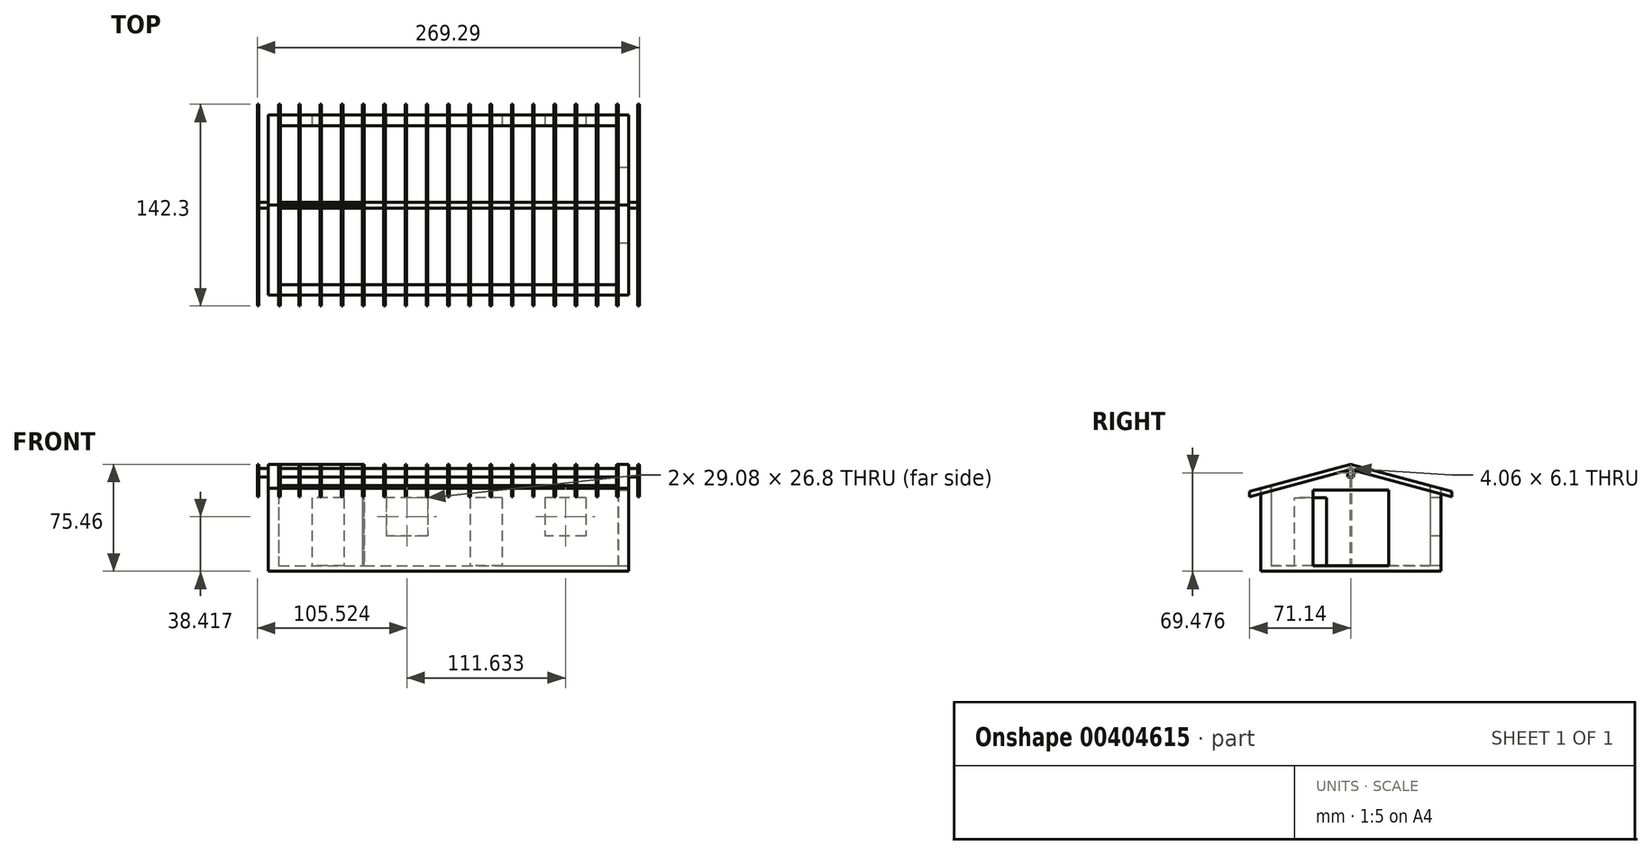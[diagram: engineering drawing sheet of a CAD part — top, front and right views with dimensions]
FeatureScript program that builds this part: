
annotation { "Feature Type Name" : "Feature", "Feature Type Description" : "" }
export const myFeature = defineFeature(function(context is Context, id is Id, definition is map)
    precondition{}
    {
        {
            var Q0;
            Q0=qCreatedBy(makeId("Top.planeOp"),FACE);
            var sketch = newSketch(context, id + "F0", { "sketchPlane" : qUnion([Q0])});
            skLineSegment(sketch, "E0.bottom", {"start": v(0, 0) * mm, "end": v(-254, 0) * mm});
            skLineSegment(sketch, "E0.top", {"start": v(0, 127) * mm, "end": v(-254, 127) * mm});
            skLineSegment(sketch, "E0.left", {"start": v(0, 0) * mm, "end": v(0, 127) * mm});
            skLineSegment(sketch, "E0.right", {"start": v(-254, 0) * mm, "end": v(-254, 127) * mm});
            skLineSegment(sketch, "E1.bottom", {"start": v(-7.37, 7.37) * mm, "end": v(-186.39, 7.37) * mm});
            skLineSegment(sketch, "E1.top", {"start": v(-7.37, 119.63) * mm, "end": v(-186.39, 119.63) * mm});
            skLineSegment(sketch, "E1.left", {"start": v(-7.37, 7.37) * mm, "end": v(-7.37, 119.63) * mm});
            skLineSegment(sketch, "E1.right", {"start": v(-246.63, 7.37) * mm, "end": v(-246.63, 62.86) * mm});
            skLineSegment(sketch, "E2", {"start": v(-186.39, 119.63) * mm, "end": v(-186.39, 7.37) * mm});
            skLineSegment(sketch, "E3", {"start": v(-187.53, 7.37) * mm, "end": v(-187.53, 62.86) * mm});
            skLineSegment(sketch, "E4", {"start": v(-187.53, 64) * mm, "end": v(-246.63, 64) * mm});
            skLineSegment(sketch, "E5", {"start": v(-246.63, 62.86) * mm, "end": v(-187.53, 62.86) * mm});
            skLineSegment(sketch, "E6.trimOffspring", {"start": v(-187.53, 64) * mm, "end": v(-187.53, 119.63) * mm});
            skLineSegment(sketch, "E7.trimOffspring", {"start": v(-187.53, 7.37) * mm, "end": v(-246.63, 7.37) * mm});
            skLineSegment(sketch, "E8.trimOffspring", {"start": v(-187.53, 119.63) * mm, "end": v(-246.63, 119.63) * mm});
            skLineSegment(sketch, "E9.trimOffspring", {"start": v(-246.63, 64) * mm, "end": v(-246.63, 119.63) * mm});
            skSolve(sketch);
        }
        {
            var Q0;
            Q0 = qSketchRegion(id + "F0", true);
            var Q1;
            Q1=makeQuery(id+"F0.imprint","IMPRINT",FACE,{"disambiguationData":[TD([[makeQuery(id+"F0.imprint","IMPRINT",EDGE,{"derivedFrom":sQuery(id+"F0.wireOp",EDGE,"E1.bottom")}),-1.0]])]});
            var Q2;
            Q2=makeQuery(id+"F0.imprint","IMPRINT",FACE,{"disambiguationData":[TD([[makeQuery(id+"F0.imprint","IMPRINT",EDGE,{"derivedFrom":sQuery(id+"F0.wireOp",EDGE,"E4")}),-1.0]])]});
            var Q3;
            Q3=makeQuery(id+"F0.imprint","IMPRINT",FACE,{"disambiguationData":[TD([[makeQuery(id+"F0.imprint","IMPRINT",EDGE,{"derivedFrom":sQuery(id+"F0.wireOp",EDGE,"E1.right")}),-1.0]])]});
            extrude(context, id + "F1", {"entities" : qUnion([Q0, Q1, Q2, Q3]), "depth" : 3.8 * mm});
        }
        {
            var Q0;
            Q0 = qSketchRegion(id + "F0", true);
            extrude(context, id + "F2", {"entities" : qUnion([Q0]), "operationType" : NewBodyOperationType.ADD, "depth" : 76.2 * mm});
        }
        {
            var Q0;
            Q0=qCreatedBy(makeId("Right.planeOp"),FACE);
            var sketch = newSketch(context, id + "F3", { "sketchPlane" : qUnion([Q0])});
            skLineSegment(sketch, "E10", {"start": v(0, 58.42) * mm, "end": v(63.5, 75.43) * mm});
            skLineSegment(sketch, "E11", {"start": v(63.5, 75.43) * mm, "end": v(127, 58.42) * mm});
            skLineSegment(sketch, "E12", {"start": v(127, 58.42) * mm, "end": v(127, 0) * mm});
            skLineSegment(sketch, "E13", {"start": v(127, 0) * mm, "end": v(0, 0) * mm});
            skLineSegment(sketch, "E14", {"start": v(0, 0) * mm, "end": v(0, 58.42) * mm});
            skLineSegment(sketch, "E15", {"start": v(0, 58.42) * mm, "end": v(0, 83.76) * mm});
            skLineSegment(sketch, "E16", {"start": v(0, 83.76) * mm, "end": v(127, 83.76) * mm});
            skLineSegment(sketch, "E17", {"start": v(127, 83.76) * mm, "end": v(127, 58.42) * mm});
            skLineSegment(sketch, "E18.bottom", {"start": v(36.83, 3.81) * mm, "end": v(90.17, 3.81) * mm});
            skLineSegment(sketch, "E18.top", {"start": v(36.83, 57.15) * mm, "end": v(90.17, 57.15) * mm});
            skLineSegment(sketch, "E18.left", {"start": v(36.83, 3.81) * mm, "end": v(36.83, 57.15) * mm});
            skLineSegment(sketch, "E18.right", {"start": v(90.17, 3.81) * mm, "end": v(90.17, 57.15) * mm});
            skLineSegment(sketch, "E19.bottom", {"start": v(61.47, 72.52) * mm, "end": v(65.53, 72.52) * mm});
            skLineSegment(sketch, "E19.top", {"start": v(61.47, 66.43) * mm, "end": v(65.53, 66.43) * mm});
            skLineSegment(sketch, "E19.left", {"start": v(61.47, 72.52) * mm, "end": v(61.47, 66.43) * mm});
            skLineSegment(sketch, "E19.right", {"start": v(65.53, 72.52) * mm, "end": v(65.53, 66.43) * mm});
            skSolve(sketch);
        }
        {
            var Q0;
            Q0=makeQuery(id+"F3.imprint","IMPRINT",FACE,{"disambiguationData":[TD([[makeQuery(id+"F3.imprint","IMPRINT",EDGE,{"derivedFrom":sQuery(id+"F3.wireOp",EDGE,"E10")}),1.0]])]});
            extrude(context, id + "F4", {"entities" : qUnion([Q0]), "operationType" : NewBodyOperationType.REMOVE, "oppositeDirection" : true, "depth" : 254 * mm});
        }
        {
            var Q0;
            Q0=makeQuery(id+"F3.imprint","IMPRINT",FACE,{"disambiguationData":[TD([[makeQuery(id+"F3.imprint","IMPRINT",EDGE,{"derivedFrom":sQuery(id+"F3.wireOp",EDGE,"CqusFpdj-rhDA-VQEZ-rAuY-6c3tKg3UXa0b.bottom")}),1.0]])]});
            var Q1;
            Q1=makeQuery(id+"F3.imprint","IMPRINT",FACE,{"disambiguationData":[TD([[makeQuery(id+"F3.imprint","IMPRINT",EDGE,{"derivedFrom":sQuery(id+"F3.wireOp",EDGE,"E18.bottom")}),1.0]])]});
            extrude(context, id + "F5", {"entities" : qUnion([Q0, Q1]), "operationType" : NewBodyOperationType.REMOVE, "oppositeDirection" : true, "depth" : 7.37 * mm});
        }
        {
            var Q0;
            Q0=qCreatedBy(makeId("Front.planeOp"),FACE);
            var sketch = newSketch(context, id + "F6", { "sketchPlane" : qUnion([Q0])});
            skLineSegment(sketch, "E20.bottom", {"start": v(-29.97, 51.82) * mm, "end": v(-59.06, 51.82) * mm});
            skLineSegment(sketch, "E20.top", {"start": v(-29.97, 25.02) * mm, "end": v(-59.06, 25.02) * mm});
            skLineSegment(sketch, "E20.left", {"start": v(-29.97, 51.82) * mm, "end": v(-29.97, 25.02) * mm});
            skLineSegment(sketch, "E20.right", {"start": v(-59.06, 51.82) * mm, "end": v(-59.06, 25.02) * mm});
            skLineSegment(sketch, "E21.bottom", {"start": v(-89.03, 51.82) * mm, "end": v(-111.63, 51.82) * mm});
            skLineSegment(sketch, "E21.top", {"start": v(-89.03, 3.81) * mm, "end": v(-111.63, 3.8) * mm});
            skLineSegment(sketch, "E21.left", {"start": v(-89.03, 51.82) * mm, "end": v(-89.03, 3.81) * mm});
            skLineSegment(sketch, "E21.right", {"start": v(-111.63, 51.82) * mm, "end": v(-111.63, 3.81) * mm});
            skLineSegment(sketch, "E22.bottom", {"start": v(-141.6, 51.82) * mm, "end": v(-170.69, 51.82) * mm});
            skLineSegment(sketch, "E22.top", {"start": v(-141.6, 25.02) * mm, "end": v(-170.69, 25.02) * mm});
            skLineSegment(sketch, "E22.left", {"start": v(-141.6, 51.82) * mm, "end": v(-141.6, 25.02) * mm});
            skLineSegment(sketch, "E22.right", {"start": v(-170.69, 51.82) * mm, "end": v(-170.69, 25.02) * mm});
            skLineSegment(sketch, "E23.bottom", {"start": v(-200.66, 51.82) * mm, "end": v(-223.27, 51.82) * mm});
            skLineSegment(sketch, "E23.top", {"start": v(-200.66, 3.81) * mm, "end": v(-223.27, 3.8) * mm});
            skLineSegment(sketch, "E23.left", {"start": v(-200.66, 51.82) * mm, "end": v(-200.66, 3.81) * mm});
            skLineSegment(sketch, "E23.right", {"start": v(-223.27, 51.82) * mm, "end": v(-223.27, 3.8) * mm});
            skSolve(sketch);
        }
        {
            var Q0;
            Q0 = qSketchRegion(id + "F6", true);
            extrude(context, id + "F7", {"entities" : qUnion([Q0]), "operationType" : NewBodyOperationType.REMOVE, "oppositeDirection" : true, "depth" : 127 * mm, "hasSecondDirection" : true, "secondDirectionOppositeDirection" : true, "secondDirectionDepth" : 119.38 * mm});
        }
        {
            var Q0;
            Q0=makeQuery(id+"F2.opExtrude","SWEPT_FACE",FACE,{"disambiguationData":[OSD([sQuery(id+"F0.wireOp",EDGE,"E2")])]});
            var sketch = newSketch(context, id + "F8", { "sketchPlane" : qUnion([Q0])});
            skLineSegment(sketch, "E24.bottom", {"start": v(23.88, 3.81) * mm, "end": v(46.48, 3.81) * mm});
            skLineSegment(sketch, "E24.top", {"start": v(23.88, 51.82) * mm, "end": v(46.48, 51.82) * mm});
            skLineSegment(sketch, "E24.left", {"start": v(23.88, 3.81) * mm, "end": v(23.88, 51.82) * mm});
            skLineSegment(sketch, "E24.right", {"start": v(46.48, 3.81) * mm, "end": v(46.48, 51.82) * mm});
            skSolve(sketch);
        }
        {
            var Q0;
            Q0 = qSketchRegion(id + "F8", true);
            extrude(context, id + "F9", {"entities" : qUnion([Q0]), "operationType" : NewBodyOperationType.REMOVE, "oppositeDirection" : true, "depth" : 1.27 * mm});
        }
        {
            var Q0;
            Q0=makeQuery(id+"F3.imprint","IMPRINT",FACE,{"disambiguationData":[TD([[makeQuery(id+"F3.imprint","IMPRINT",EDGE,{"derivedFrom":sQuery(id+"F3.wireOp",EDGE,"E19.bottom")}),-1.0]])]});
            extrude(context, id + "F10", {"entities" : qUnion([Q0]), "operationType" : NewBodyOperationType.ADD, "oppositeDirection" : true, "depth" : 261.62 * mm, "hasSecondDirection" : true, "secondDirectionOppositeDirection" : false, "secondDirectionDepth" : 7.62 * mm});
        }
        {
            var Q0;
            Q0=makeQuery(id+"F4.boolean.opBoolean","COPY",FACE,{"derivedFrom":makeQuery(id+"F4.opExtrude","SWEPT_FACE",FACE,{"disambiguationData":[OSD([sQuery(id+"F3.wireOp",EDGE,"E11")])]})});
            var sketch = newSketch(context, id + "F11", { "sketchPlane" : qUnion([Q0])});
            skLineSegment(sketch, "E25.bottom", {"start": v(7.62, 41.81) * mm, "end": v(6.48, 41.81) * mm});
            skLineSegment(sketch, "E25.top", {"start": v(7.62, 125.63) * mm, "end": v(6.48, 125.63) * mm});
            skLineSegment(sketch, "E25.left", {"start": v(7.62, 41.81) * mm, "end": v(7.62, 125.63) * mm});
            skLineSegment(sketch, "E25.right", {"start": v(6.48, 41.81) * mm, "end": v(6.48, 125.63) * mm});
            skLineSegment(sketch, "E26.bottom", {"start": v(-7.37, 41.81) * mm, "end": v(-8.5, 41.81) * mm});
            skLineSegment(sketch, "E26.top", {"start": v(-7.37, 125.63) * mm, "end": v(-8.5, 125.63) * mm});
            skLineSegment(sketch, "E26.left", {"start": v(-7.37, 41.81) * mm, "end": v(-7.37, 125.63) * mm});
            skLineSegment(sketch, "E26.right", {"start": v(-8.5, 41.81) * mm, "end": v(-8.5, 125.63) * mm});
            skLineSegment(sketch, "E27.bottom", {"start": v(-21.54, 41.81) * mm, "end": v(-22.68, 41.81) * mm});
            skLineSegment(sketch, "E27.top", {"start": v(-21.54, 125.63) * mm, "end": v(-22.68, 125.63) * mm});
            skLineSegment(sketch, "E27.left", {"start": v(-21.54, 41.81) * mm, "end": v(-21.54, 125.63) * mm});
            skLineSegment(sketch, "E27.right", {"start": v(-22.68, 41.81) * mm, "end": v(-22.68, 125.63) * mm});
            skLineSegment(sketch, "E28.bottom", {"start": v(-36.53, 41.81) * mm, "end": v(-37.67, 41.81) * mm});
            skLineSegment(sketch, "E28.top", {"start": v(-36.53, 125.63) * mm, "end": v(-37.67, 125.63) * mm});
            skLineSegment(sketch, "E28.left", {"start": v(-36.53, 41.81) * mm, "end": v(-36.53, 125.63) * mm});
            skLineSegment(sketch, "E28.right", {"start": v(-37.67, 41.81) * mm, "end": v(-37.67, 125.63) * mm});
            skLineSegment(sketch, "E29.bottom", {"start": v(-51.51, 41.81) * mm, "end": v(-52.65, 41.81) * mm});
            skLineSegment(sketch, "E29.top", {"start": v(-51.51, 125.63) * mm, "end": v(-52.65, 125.63) * mm});
            skLineSegment(sketch, "E29.left", {"start": v(-51.51, 41.81) * mm, "end": v(-51.51, 125.63) * mm});
            skLineSegment(sketch, "E29.right", {"start": v(-52.65, 41.81) * mm, "end": v(-52.65, 125.63) * mm});
            skLineSegment(sketch, "E30.bottom", {"start": v(-66.5, 41.81) * mm, "end": v(-67.64, 41.81) * mm});
            skLineSegment(sketch, "E30.top", {"start": v(-66.5, 125.63) * mm, "end": v(-67.64, 125.63) * mm});
            skLineSegment(sketch, "E30.left", {"start": v(-66.5, 41.81) * mm, "end": v(-66.5, 125.63) * mm});
            skLineSegment(sketch, "E30.right", {"start": v(-67.64, 41.81) * mm, "end": v(-67.64, 125.63) * mm});
            skLineSegment(sketch, "E31.bottom", {"start": v(-81.48, 41.81) * mm, "end": v(-82.63, 41.81) * mm});
            skLineSegment(sketch, "E31.top", {"start": v(-81.48, 125.63) * mm, "end": v(-82.63, 125.63) * mm});
            skLineSegment(sketch, "E31.left", {"start": v(-81.48, 41.81) * mm, "end": v(-81.48, 125.63) * mm});
            skLineSegment(sketch, "E31.right", {"start": v(-82.63, 41.81) * mm, "end": v(-82.63, 125.63) * mm});
            skLineSegment(sketch, "E32.bottom", {"start": v(-96.47, 41.81) * mm, "end": v(-97.61, 41.81) * mm});
            skLineSegment(sketch, "E32.top", {"start": v(-96.47, 125.63) * mm, "end": v(-97.61, 125.63) * mm});
            skLineSegment(sketch, "E32.left", {"start": v(-96.47, 41.81) * mm, "end": v(-96.47, 125.63) * mm});
            skLineSegment(sketch, "E32.right", {"start": v(-97.61, 41.81) * mm, "end": v(-97.61, 125.63) * mm});
            skLineSegment(sketch, "E33.bottom", {"start": v(-111.46, 41.81) * mm, "end": v(-112.6, 41.81) * mm});
            skLineSegment(sketch, "E33.top", {"start": v(-111.46, 125.63) * mm, "end": v(-112.6, 125.63) * mm});
            skLineSegment(sketch, "E33.left", {"start": v(-111.46, 41.81) * mm, "end": v(-111.46, 125.63) * mm});
            skLineSegment(sketch, "E33.right", {"start": v(-112.6, 41.81) * mm, "end": v(-112.6, 125.63) * mm});
            skLineSegment(sketch, "E34.bottom", {"start": v(-126.44, 41.81) * mm, "end": v(-127.58, 41.81) * mm});
            skLineSegment(sketch, "E34.top", {"start": v(-126.44, 125.63) * mm, "end": v(-127.58, 125.63) * mm});
            skLineSegment(sketch, "E34.left", {"start": v(-126.44, 41.81) * mm, "end": v(-126.44, 125.63) * mm});
            skLineSegment(sketch, "E34.right", {"start": v(-127.58, 41.81) * mm, "end": v(-127.58, 125.63) * mm});
            skLineSegment(sketch, "E35.bottom", {"start": v(-141.43, 41.81) * mm, "end": v(-142.57, 41.81) * mm});
            skLineSegment(sketch, "E35.top", {"start": v(-141.43, 125.63) * mm, "end": v(-142.57, 125.63) * mm});
            skLineSegment(sketch, "E35.left", {"start": v(-141.43, 41.81) * mm, "end": v(-141.43, 125.63) * mm});
            skLineSegment(sketch, "E35.right", {"start": v(-142.57, 41.81) * mm, "end": v(-142.57, 125.63) * mm});
            skLineSegment(sketch, "E36.bottom", {"start": v(-156.41, 41.81) * mm, "end": v(-157.56, 41.81) * mm});
            skLineSegment(sketch, "E36.top", {"start": v(-156.41, 125.63) * mm, "end": v(-157.56, 125.63) * mm});
            skLineSegment(sketch, "E36.left", {"start": v(-156.41, 41.81) * mm, "end": v(-156.41, 125.63) * mm});
            skLineSegment(sketch, "E36.right", {"start": v(-157.56, 41.81) * mm, "end": v(-157.56, 125.63) * mm});
            skLineSegment(sketch, "E37.bottom", {"start": v(-171.4, 41.81) * mm, "end": v(-172.54, 41.81) * mm});
            skLineSegment(sketch, "E37.top", {"start": v(-171.4, 125.63) * mm, "end": v(-172.54, 125.63) * mm});
            skLineSegment(sketch, "E37.left", {"start": v(-171.4, 41.81) * mm, "end": v(-171.4, 125.63) * mm});
            skLineSegment(sketch, "E37.right", {"start": v(-172.54, 41.81) * mm, "end": v(-172.54, 125.63) * mm});
            skLineSegment(sketch, "E38.bottom", {"start": v(-186.39, 41.81) * mm, "end": v(-187.53, 41.81) * mm});
            skLineSegment(sketch, "E38.top", {"start": v(-186.39, 125.63) * mm, "end": v(-187.53, 125.63) * mm});
            skLineSegment(sketch, "E38.left", {"start": v(-186.39, 41.81) * mm, "end": v(-186.39, 125.63) * mm});
            skLineSegment(sketch, "E38.right", {"start": v(-187.53, 41.81) * mm, "end": v(-187.53, 125.63) * mm});
            skLineSegment(sketch, "E39.bottom", {"start": v(-201.37, 41.81) * mm, "end": v(-202.51, 41.81) * mm});
            skLineSegment(sketch, "E39.top", {"start": v(-201.37, 125.63) * mm, "end": v(-202.51, 125.63) * mm});
            skLineSegment(sketch, "E39.left", {"start": v(-201.37, 41.81) * mm, "end": v(-201.37, 125.63) * mm});
            skLineSegment(sketch, "E39.right", {"start": v(-202.51, 41.81) * mm, "end": v(-202.51, 125.63) * mm});
            skLineSegment(sketch, "E40.bottom", {"start": v(-216.36, 41.81) * mm, "end": v(-217.5, 41.81) * mm});
            skLineSegment(sketch, "E40.top", {"start": v(-216.36, 125.63) * mm, "end": v(-217.5, 125.63) * mm});
            skLineSegment(sketch, "E40.left", {"start": v(-216.36, 41.81) * mm, "end": v(-216.36, 125.63) * mm});
            skLineSegment(sketch, "E40.right", {"start": v(-217.5, 41.81) * mm, "end": v(-217.5, 125.63) * mm});
            skLineSegment(sketch, "E41.bottom", {"start": v(-231.34, 41.81) * mm, "end": v(-232.49, 41.81) * mm});
            skLineSegment(sketch, "E41.top", {"start": v(-231.34, 125.63) * mm, "end": v(-232.49, 125.63) * mm});
            skLineSegment(sketch, "E41.left", {"start": v(-231.34, 41.81) * mm, "end": v(-231.34, 125.63) * mm});
            skLineSegment(sketch, "E41.right", {"start": v(-232.49, 41.81) * mm, "end": v(-232.49, 125.63) * mm});
            skLineSegment(sketch, "E42.bottom", {"start": v(-245.5, 41.81) * mm, "end": v(-246.63, 41.81) * mm});
            skLineSegment(sketch, "E42.top", {"start": v(-245.5, 125.63) * mm, "end": v(-246.63, 125.63) * mm});
            skLineSegment(sketch, "E42.left", {"start": v(-245.5, 41.81) * mm, "end": v(-245.5, 125.63) * mm});
            skLineSegment(sketch, "E42.right", {"start": v(-246.63, 41.81) * mm, "end": v(-246.63, 125.63) * mm});
            skLineSegment(sketch, "E43.bottom", {"start": v(-260.53, 41.81) * mm, "end": v(-261.67, 41.81) * mm});
            skLineSegment(sketch, "E43.top", {"start": v(-260.53, 125.63) * mm, "end": v(-261.67, 125.63) * mm});
            skLineSegment(sketch, "E43.left", {"start": v(-260.53, 41.81) * mm, "end": v(-260.53, 125.63) * mm});
            skLineSegment(sketch, "E43.right", {"start": v(-261.67, 41.81) * mm, "end": v(-261.67, 125.63) * mm});
            skSolve(sketch);
        }
        {
            var Q0;
            Q0 = qSketchRegion(id + "F11", true);
            extrude(context, id + "F12", {"entities" : qUnion([Q0]), "operationType" : NewBodyOperationType.ADD, "oppositeDirection" : true, "depth" : 3.68 * mm, "hasSecondDirection" : true, "secondDirectionOppositeDirection" : false, "secondDirectionDepth" : 0.03 * mm});
        }
        {
            var Q0;
            Q0=makeQuery(id+"F12.boolean.opBoolean","MERGE",FACE,{"derivedFrom":[makeQuery(id+"F10.opExtrude","CAP_FACE",FACE,{"disambiguationData":[OSD([sQuery(id+"F3.wireOp",EDGE,"E19.bottom"),sQuery(id+"F3.wireOp",EDGE,"E19.top"),sQuery(id+"F3.wireOp",EDGE,"E19.left"),sQuery(id+"F3.wireOp",EDGE,"E19.right")])],"isStart":true}),makeQuery(id+"F12.opExtrude","SWEPT_FACE",FACE,{"disambiguationData":[OSD([sQuery(id+"F11.wireOp",EDGE,"E25.left")])]})]});
            var sketch = newSketch(context, id + "F13", { "sketchPlane" : qUnion([Q0])});
            skLineSegment(sketch, "E44", {"start": v(134.66, 56.4) * mm, "end": v(134.66, 52.56) * mm});
            skLineSegment(sketch, "E45", {"start": v(134.66, 52.56) * mm, "end": v(146.92, 49.27) * mm});
            skLineSegment(sketch, "E46", {"start": v(146.92, 49.27) * mm, "end": v(146.92, 53.1) * mm});
            skLineSegment(sketch, "E47", {"start": v(146.92, 53.1) * mm, "end": v(134.66, 56.4) * mm});
            skSolve(sketch);
        }
        {
            var Q0;
            Q0 = qSketchRegion(id + "F13", true);
            extrude(context, id + "F14", {"entities" : qUnion([Q0]), "operationType" : NewBodyOperationType.REMOVE, "oppositeDirection" : true, "depth" : 271.78 * mm});
        }
        {
            var Q0;
            Q0=makeQuery(id+"F4.boolean.opBoolean","COPY",FACE,{"derivedFrom":makeQuery(id+"F4.opExtrude","SWEPT_FACE",FACE,{"disambiguationData":[OSD([sQuery(id+"F3.wireOp",EDGE,"E10")])]})});
            var sketch = newSketch(context, id + "F15", { "sketchPlane" : qUnion([Q0])});
            skLineSegment(sketch, "E48.bottom", {"start": v(7.62, -2.96) * mm, "end": v(6.48, -2.96) * mm});
            skLineSegment(sketch, "E48.top", {"start": v(7.62, 80.86) * mm, "end": v(6.48, 80.86) * mm});
            skLineSegment(sketch, "E48.left", {"start": v(7.62, -2.96) * mm, "end": v(7.62, 80.86) * mm});
            skLineSegment(sketch, "E48.right", {"start": v(6.48, -2.96) * mm, "end": v(6.48, 80.86) * mm});
            skLineSegment(sketch, "E49.bottom", {"start": v(-7.37, -2.96) * mm, "end": v(-8.5, -2.96) * mm});
            skLineSegment(sketch, "E49.top", {"start": v(-7.37, 80.86) * mm, "end": v(-8.5, 80.86) * mm});
            skLineSegment(sketch, "E49.left", {"start": v(-7.37, -2.96) * mm, "end": v(-7.37, 80.86) * mm});
            skLineSegment(sketch, "E49.right", {"start": v(-8.5, -2.96) * mm, "end": v(-8.5, 80.86) * mm});
            skLineSegment(sketch, "E50.bottom", {"start": v(-21.54, -2.96) * mm, "end": v(-22.68, -2.96) * mm});
            skLineSegment(sketch, "E50.top", {"start": v(-21.54, 80.86) * mm, "end": v(-22.68, 80.86) * mm});
            skLineSegment(sketch, "E50.left", {"start": v(-21.54, -2.96) * mm, "end": v(-21.54, 80.86) * mm});
            skLineSegment(sketch, "E50.right", {"start": v(-22.68, -2.96) * mm, "end": v(-22.68, 80.86) * mm});
            skLineSegment(sketch, "E51.bottom", {"start": v(-36.53, -2.96) * mm, "end": v(-37.67, -2.96) * mm});
            skLineSegment(sketch, "E51.top", {"start": v(-36.53, 80.86) * mm, "end": v(-37.67, 80.86) * mm});
            skLineSegment(sketch, "E51.left", {"start": v(-36.53, -2.96) * mm, "end": v(-36.53, 80.86) * mm});
            skLineSegment(sketch, "E51.right", {"start": v(-37.67, -2.96) * mm, "end": v(-37.67, 80.86) * mm});
            skLineSegment(sketch, "E52.bottom", {"start": v(-51.51, -2.96) * mm, "end": v(-52.65, -2.96) * mm});
            skLineSegment(sketch, "E52.top", {"start": v(-51.51, 80.86) * mm, "end": v(-52.65, 80.86) * mm});
            skLineSegment(sketch, "E52.left", {"start": v(-51.51, -2.96) * mm, "end": v(-51.51, 80.86) * mm});
            skLineSegment(sketch, "E52.right", {"start": v(-52.65, -2.96) * mm, "end": v(-52.65, 80.86) * mm});
            skLineSegment(sketch, "E53.bottom", {"start": v(-66.5, -2.96) * mm, "end": v(-67.64, -2.96) * mm});
            skLineSegment(sketch, "E53.top", {"start": v(-66.5, 80.86) * mm, "end": v(-67.64, 80.86) * mm});
            skLineSegment(sketch, "E53.left", {"start": v(-66.5, -2.96) * mm, "end": v(-66.5, 80.86) * mm});
            skLineSegment(sketch, "E53.right", {"start": v(-67.64, -2.96) * mm, "end": v(-67.64, 80.86) * mm});
            skLineSegment(sketch, "E54.bottom", {"start": v(-81.48, -2.96) * mm, "end": v(-82.63, -2.96) * mm});
            skLineSegment(sketch, "E54.top", {"start": v(-81.48, 80.86) * mm, "end": v(-82.63, 80.86) * mm});
            skLineSegment(sketch, "E54.left", {"start": v(-81.48, -2.96) * mm, "end": v(-81.48, 80.86) * mm});
            skLineSegment(sketch, "E54.right", {"start": v(-82.63, -2.96) * mm, "end": v(-82.63, 80.86) * mm});
            skLineSegment(sketch, "E55.bottom", {"start": v(-96.47, -2.96) * mm, "end": v(-97.61, -2.96) * mm});
            skLineSegment(sketch, "E55.top", {"start": v(-96.47, 80.86) * mm, "end": v(-97.61, 80.86) * mm});
            skLineSegment(sketch, "E55.left", {"start": v(-96.47, -2.96) * mm, "end": v(-96.47, 80.86) * mm});
            skLineSegment(sketch, "E55.right", {"start": v(-97.61, -2.96) * mm, "end": v(-97.61, 80.86) * mm});
            skLineSegment(sketch, "E56.bottom", {"start": v(-111.46, -2.96) * mm, "end": v(-112.6, -2.96) * mm});
            skLineSegment(sketch, "E56.top", {"start": v(-111.46, 80.86) * mm, "end": v(-112.6, 80.86) * mm});
            skLineSegment(sketch, "E56.left", {"start": v(-111.46, -2.96) * mm, "end": v(-111.46, 80.86) * mm});
            skLineSegment(sketch, "E56.right", {"start": v(-112.6, -2.96) * mm, "end": v(-112.6, 80.86) * mm});
            skLineSegment(sketch, "E57.bottom", {"start": v(-126.44, -2.96) * mm, "end": v(-127.58, -2.96) * mm});
            skLineSegment(sketch, "E57.top", {"start": v(-126.44, 80.86) * mm, "end": v(-127.58, 80.86) * mm});
            skLineSegment(sketch, "E57.left", {"start": v(-126.44, -2.96) * mm, "end": v(-126.44, 80.86) * mm});
            skLineSegment(sketch, "E57.right", {"start": v(-127.58, -2.96) * mm, "end": v(-127.58, 80.86) * mm});
            skLineSegment(sketch, "E58.bottom", {"start": v(-141.43, -2.96) * mm, "end": v(-142.57, -2.96) * mm});
            skLineSegment(sketch, "E58.top", {"start": v(-141.43, 80.86) * mm, "end": v(-142.57, 80.86) * mm});
            skLineSegment(sketch, "E58.left", {"start": v(-141.43, -2.96) * mm, "end": v(-141.43, 80.86) * mm});
            skLineSegment(sketch, "E58.right", {"start": v(-142.57, -2.96) * mm, "end": v(-142.57, 80.86) * mm});
            skLineSegment(sketch, "E59.bottom", {"start": v(-156.41, -2.96) * mm, "end": v(-157.56, -2.96) * mm});
            skLineSegment(sketch, "E59.top", {"start": v(-156.41, 80.86) * mm, "end": v(-157.56, 80.86) * mm});
            skLineSegment(sketch, "E59.left", {"start": v(-156.41, -2.96) * mm, "end": v(-156.41, 80.86) * mm});
            skLineSegment(sketch, "E59.right", {"start": v(-157.56, -2.96) * mm, "end": v(-157.56, 80.86) * mm});
            skLineSegment(sketch, "E60.bottom", {"start": v(-171.4, -2.96) * mm, "end": v(-172.54, -2.96) * mm});
            skLineSegment(sketch, "E60.top", {"start": v(-171.4, 80.86) * mm, "end": v(-172.54, 80.86) * mm});
            skLineSegment(sketch, "E60.left", {"start": v(-171.4, -2.96) * mm, "end": v(-171.4, 80.86) * mm});
            skLineSegment(sketch, "E60.right", {"start": v(-172.54, -2.96) * mm, "end": v(-172.54, 80.86) * mm});
            skLineSegment(sketch, "E61.bottom", {"start": v(-186.39, -2.96) * mm, "end": v(-187.53, -2.96) * mm});
            skLineSegment(sketch, "E61.top", {"start": v(-186.39, 80.86) * mm, "end": v(-187.53, 80.86) * mm});
            skLineSegment(sketch, "E61.left", {"start": v(-186.39, -2.96) * mm, "end": v(-186.39, 80.86) * mm});
            skLineSegment(sketch, "E61.right", {"start": v(-187.53, -2.96) * mm, "end": v(-187.53, 80.86) * mm});
            skLineSegment(sketch, "E62.bottom", {"start": v(-201.37, -2.96) * mm, "end": v(-202.51, -2.96) * mm});
            skLineSegment(sketch, "E62.top", {"start": v(-201.37, 80.86) * mm, "end": v(-202.51, 80.86) * mm});
            skLineSegment(sketch, "E62.left", {"start": v(-201.37, -2.96) * mm, "end": v(-201.37, 80.86) * mm});
            skLineSegment(sketch, "E62.right", {"start": v(-202.51, -2.96) * mm, "end": v(-202.51, 80.86) * mm});
            skLineSegment(sketch, "E63.bottom", {"start": v(-216.36, -2.96) * mm, "end": v(-217.5, -2.96) * mm});
            skLineSegment(sketch, "E63.top", {"start": v(-216.36, 80.86) * mm, "end": v(-217.5, 80.86) * mm});
            skLineSegment(sketch, "E63.left", {"start": v(-216.36, -2.96) * mm, "end": v(-216.36, 80.86) * mm});
            skLineSegment(sketch, "E63.right", {"start": v(-217.5, -2.96) * mm, "end": v(-217.5, 80.86) * mm});
            skLineSegment(sketch, "E64.bottom", {"start": v(-231.34, -2.96) * mm, "end": v(-232.49, -2.96) * mm});
            skLineSegment(sketch, "E64.top", {"start": v(-231.34, 80.86) * mm, "end": v(-232.49, 80.86) * mm});
            skLineSegment(sketch, "E64.left", {"start": v(-231.34, -2.96) * mm, "end": v(-231.34, 80.86) * mm});
            skLineSegment(sketch, "E64.right", {"start": v(-232.49, -2.96) * mm, "end": v(-232.49, 80.86) * mm});
            skLineSegment(sketch, "E65.bottom", {"start": v(-245.5, -2.96) * mm, "end": v(-246.63, -2.96) * mm});
            skLineSegment(sketch, "E65.top", {"start": v(-245.5, 80.86) * mm, "end": v(-246.63, 80.86) * mm});
            skLineSegment(sketch, "E65.left", {"start": v(-245.5, -2.96) * mm, "end": v(-245.5, 80.86) * mm});
            skLineSegment(sketch, "E65.right", {"start": v(-246.63, -2.96) * mm, "end": v(-246.63, 80.86) * mm});
            skLineSegment(sketch, "E66.bottom", {"start": v(-260.53, -2.96) * mm, "end": v(-261.67, -2.96) * mm});
            skLineSegment(sketch, "E66.top", {"start": v(-260.53, 80.86) * mm, "end": v(-261.67, 80.86) * mm});
            skLineSegment(sketch, "E66.left", {"start": v(-260.53, -2.96) * mm, "end": v(-260.53, 80.86) * mm});
            skLineSegment(sketch, "E66.right", {"start": v(-261.67, -2.96) * mm, "end": v(-261.67, 80.86) * mm});
            skSolve(sketch);
        }
        {
            var Q0;
            Q0 = qSketchRegion(id + "F15", true);
            extrude(context, id + "F16", {"entities" : qUnion([Q0]), "operationType" : NewBodyOperationType.ADD, "oppositeDirection" : true, "depth" : 3.68 * mm, "hasSecondDirection" : true, "secondDirectionOppositeDirection" : false, "secondDirectionDepth" : 0.03 * mm});
        }
        {
            var Q0;
            Q0=makeQuery(id+"F16.boolean.opBoolean","MERGE",FACE,{"derivedFrom":[makeQuery(id+"F12.boolean.opBoolean","MERGE",FACE,{"derivedFrom":[makeQuery(id+"F10.opExtrude","CAP_FACE",FACE,{"disambiguationData":[OSD([sQuery(id+"F3.wireOp",EDGE,"E19.bottom"),sQuery(id+"F3.wireOp",EDGE,"E19.top"),sQuery(id+"F3.wireOp",EDGE,"E19.left"),sQuery(id+"F3.wireOp",EDGE,"E19.right")])],"isStart":true}),makeQuery(id+"F12.opExtrude","SWEPT_FACE",FACE,{"disambiguationData":[OSD([sQuery(id+"F11.wireOp",EDGE,"E25.left")])]})]}),makeQuery(id+"F16.opExtrude","SWEPT_FACE",FACE,{"disambiguationData":[OSD([sQuery(id+"F15.wireOp",EDGE,"E48.left")])]})]});
            var sketch = newSketch(context, id + "F17", { "sketchPlane" : qUnion([Q0])});
            skLineSegment(sketch, "E67", {"start": v(-7.64, 56.4) * mm, "end": v(-7.64, 52.56) * mm});
            skLineSegment(sketch, "E68", {"start": v(-7.64, 52.56) * mm, "end": v(-19.91, 49.27) * mm});
            skLineSegment(sketch, "E69", {"start": v(-19.91, 49.27) * mm, "end": v(-19.91, 53.11) * mm});
            skLineSegment(sketch, "E70", {"start": v(-19.91, 53.11) * mm, "end": v(-7.64, 56.4) * mm});
            skSolve(sketch);
        }
        {
            var Q0;
            Q0 = qSketchRegion(id + "F17", true);
            extrude(context, id + "F18", {"entities" : qUnion([Q0]), "operationType" : NewBodyOperationType.REMOVE, "oppositeDirection" : true, "depth" : 271.78 * mm});
        }
    });
